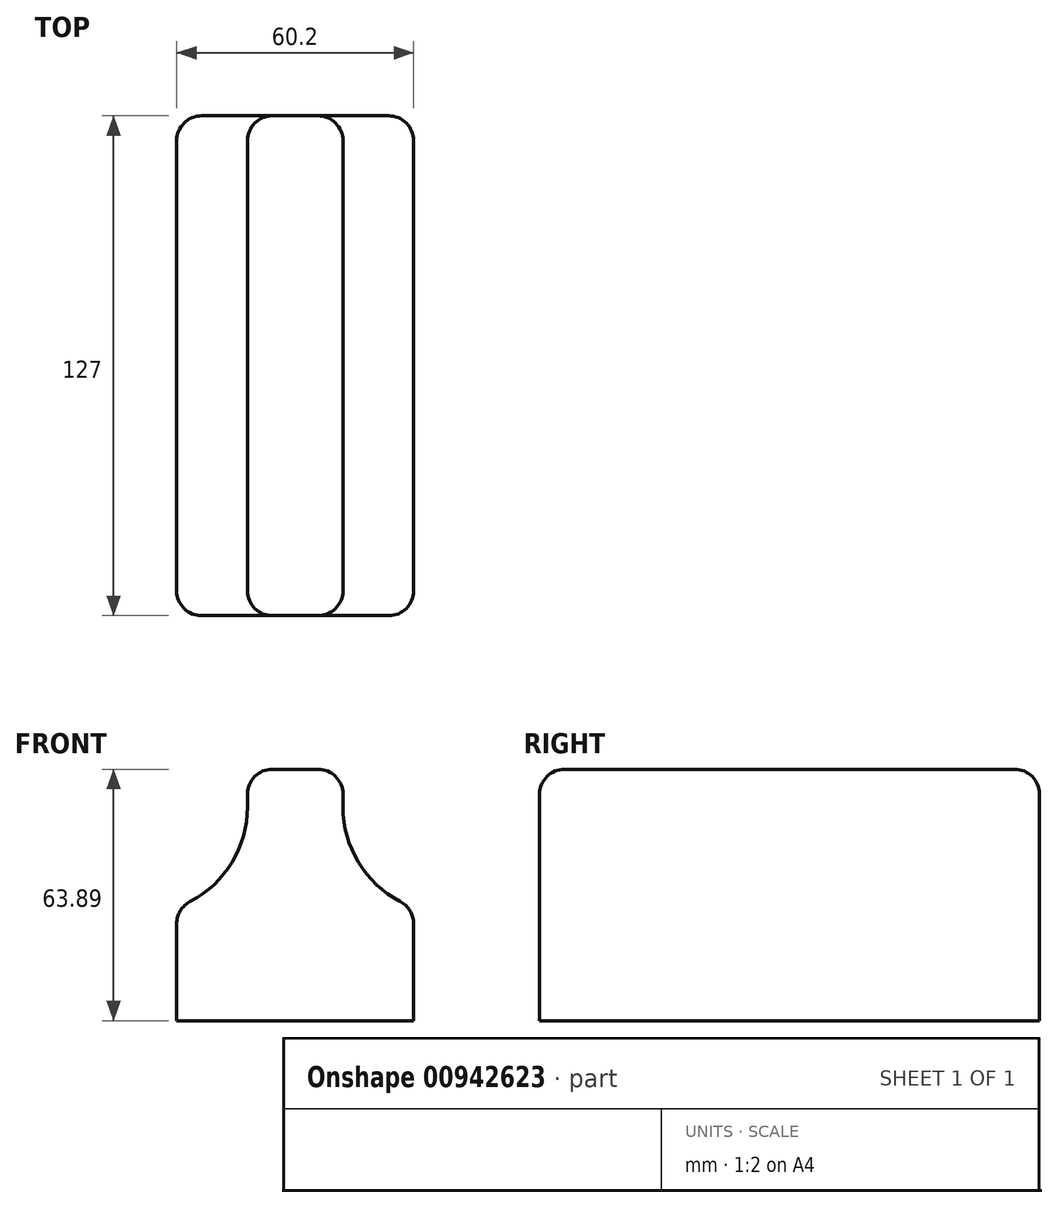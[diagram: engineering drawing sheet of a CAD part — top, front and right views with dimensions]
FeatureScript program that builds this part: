
annotation { "Feature Type Name" : "Feature", "Feature Type Description" : "" }
export const myFeature = defineFeature(function(context is Context, id is Id, definition is map)
    precondition{}
    {
        {
            var Q0;
            Q0=qCreatedBy(makeId("Front.planeOp"),FACE);
            var sketch = newSketch(context, id + "F0", { "sketchPlane" : qUnion([Q0])});
            skLineSegment(sketch, "E0.bottom", {"start": v(30.1, -14.38) * mm, "end": v(-30.1, -14.38) * mm});
            skLineSegment(sketch, "E0.top", {"start": v(30.1, 14.38) * mm, "end": v(-30.1, 14.38) * mm});
            skLineSegment(sketch, "E0.left", {"start": v(30.1, -14.38) * mm, "end": v(30.1, 14.38) * mm});
            skLineSegment(sketch, "E0.right", {"start": v(-30.1, -14.38) * mm, "end": v(-30.1, 14.38) * mm});
            skPoint(sketch, "E0.middle", {"position": v(0, 0) * mm});
            skLineSegment(sketch, "E1.bottom", {"start": v(-12.15, 39.87) * mm, "end": v(12.15, 39.87) * mm});
            skLineSegment(sketch, "E1.top", {"start": v(-12.15, 49.51) * mm, "end": v(12.15, 49.51) * mm});
            skLineSegment(sketch, "E1.left", {"start": v(-12.15, 39.87) * mm, "end": v(-12.15, 49.51) * mm});
            skLineSegment(sketch, "E1.right", {"start": v(12.15, 39.87) * mm, "end": v(12.15, 49.51) * mm});
            skPoint(sketch, "E1.middle", {"position": v(0, 44.69) * mm});
            skPoint(sketch, "E2.endSnap0", {"position": v(0, 39.87) * mm});
            skArc(sketch, "E3", {"start": v(-30.1, 14.38) * mm, "mid": v(-17.09, 24.28) * mm, "end": v(-12.15, 39.87) * mm});
            skArc(sketch, "E4", {"start": v(12.15, 39.87) * mm, "mid": v(17.09, 24.28) * mm, "end": v(30.1, 14.38) * mm});
            skSolve(sketch);
        }
        {
            var Q0;
            Q0=makeQuery(id+"F0.imprint","IMPRINT",FACE,{"disambiguationData":[TD([[makeQuery(id+"F0.imprint","IMPRINT",EDGE,{"derivedFrom":sQuery(id+"F0.wireOp",EDGE,"E0.bottom")}),-1.0]])]});
            var Q1;
            Q1=makeQuery(id+"F0.imprint","IMPRINT",FACE,{"disambiguationData":[TD([[makeQuery(id+"F0.imprint","IMPRINT",EDGE,{"derivedFrom":sQuery(id+"F0.wireOp",EDGE,"E0.top")}),-1.0]])]});
            var Q2;
            Q2=makeQuery(id+"F0.imprint","IMPRINT",FACE,{"disambiguationData":[TD([[makeQuery(id+"F0.imprint","IMPRINT",EDGE,{"derivedFrom":sQuery(id+"F0.wireOp",EDGE,"E1.bottom")}),1.0]])]});
            extrude(context, id + "F1", {"entities" : qUnion([Q0, Q1, Q2]), "endBound" : BoundingType.SYMMETRIC, "depth" : 127 * mm, "offsetDistance" : 25.4 * mm});
        }
        {
            var Q0;
            Q0=makeQuery(id+"F1.opExtrude","CAP_EDGE",EDGE,{"disambiguationData":[OSD([sQuery(id+"F0.wireOp",EDGE,"E0.right")])],"isStart":false});
            var Q1;
            Q1=makeQuery(id+"F1.opExtrude","CAP_EDGE",EDGE,{"disambiguationData":[OSD([sQuery(id+"F0.wireOp",EDGE,"E0.left")])],"isStart":false});
            var Q2;
            Q2=makeQuery(id+"F1.opExtrude","CAP_EDGE",EDGE,{"disambiguationData":[OSD([sQuery(id+"F0.wireOp",EDGE,"E0.right")])],"isStart":true});
            var Q3;
            Q3=makeQuery(id+"F1.opExtrude","CAP_EDGE",EDGE,{"disambiguationData":[OSD([sQuery(id+"F0.wireOp",EDGE,"E0.left")])],"isStart":true});
            var Q4;
            Q4=makeQuery(id+"F1.opExtrude","CAP_EDGE",EDGE,{"disambiguationData":[OSD([sQuery(id+"F0.wireOp",EDGE,"E1.top")])],"isStart":true});
            var Q5;
            Q5=makeQuery(id+"F1.opExtrude","CAP_EDGE",EDGE,{"disambiguationData":[OSD([sQuery(id+"F0.wireOp",EDGE,"E1.top")])],"isStart":false});
            var Q6;
            Q6=makeQuery(id+"F1.opExtrude","SWEPT_EDGE",EDGE,{"disambiguationData":[OSD([sQuery(id+"F0.wireOp",EDGE,"E1.top"),sQuery(id+"F0.wireOp",EDGE,"E1.right")])]});
            var Q7;
            Q7=makeQuery(id+"F1.opExtrude","SWEPT_EDGE",EDGE,{"disambiguationData":[OSD([sQuery(id+"F0.wireOp",EDGE,"E0.top"),sQuery(id+"F0.wireOp",EDGE,"E0.left"),sQuery(id+"F0.wireOp",EDGE,"E4")])]});
            var Q8;
            Q8=makeQuery(id+"F1.opExtrude","SWEPT_EDGE",EDGE,{"disambiguationData":[OSD([sQuery(id+"F0.wireOp",EDGE,"E0.top"),sQuery(id+"F0.wireOp",EDGE,"E0.right"),sQuery(id+"F0.wireOp",EDGE,"E3")])]});
            var Q9;
            Q9=makeQuery(id+"F1.opExtrude","SWEPT_EDGE",EDGE,{"disambiguationData":[OSD([sQuery(id+"F0.wireOp",EDGE,"E1.top"),sQuery(id+"F0.wireOp",EDGE,"E1.left")])]});
            var Q10;
            Q10=makeQuery(id+"F1.opExtrude","CAP_EDGE",EDGE,{"disambiguationData":[OSD([sQuery(id+"F0.wireOp",EDGE,"E3")])],"isStart":true});
            var Q11;
            Q11=makeQuery(id+"F1.opExtrude","CAP_EDGE",EDGE,{"disambiguationData":[OSD([sQuery(id+"F0.wireOp",EDGE,"E4")])],"isStart":true});
            var Q12;
            Q12=makeQuery(id+"F1.opExtrude","CAP_EDGE",EDGE,{"disambiguationData":[OSD([sQuery(id+"F0.wireOp",EDGE,"E4")])],"isStart":false});
            var Q13;
            Q13=makeQuery(id+"F1.opExtrude","CAP_EDGE",EDGE,{"disambiguationData":[OSD([sQuery(id+"F0.wireOp",EDGE,"E3")])],"isStart":false});
            fillet(context, id + "F2", {"entities" : qUnion([Q0, Q1, Q2, Q3, Q4, Q5, Q6, Q7, Q8, Q9, Q10, Q11, Q12, Q13]), "radius" : 6.35 * mm, "tangentPropagation" : true, "allowEdgeOverflow" : false});
        }
    });
